# Revit family: Hager-VOLTA-Surface_mounted-IP30-Without_Cover-Without_DIN-Hosted-CH-fr
name_source: partatom
category: Electrical Equipment
units: mm (PartAtom-declared; Revit-internal decimal feet)

## family parameters
Cut with Voids When Loaded = No
Host = Face
Maintain Annotation Orientation = Yes
Panel Configuration = Two Columns, Circuits Across
Part Type = Panelboard
Room Calculation Point = No
Round Connector Dimension = Use Diameter
Shared = No

## types (1)
- VOLTA-Surface_mounted_W305_H640_D96_12_Modular_Spacing-VA48MD
    BC_MODEL_ID = 1547148
    BC_OBJECT_ID = 513473
    BC_OBJECT_VERSION = #9
    BC_VARIANT_ID = 1174158
    Code hager = ADD-EC000214_EU
    Default Elevation = 0 mm  [stored 0 ft]
    EF000003 - mode de montage = apparent
    EF000007 - couleur = blanc
    EF000008 - largeur = 305 mm  [stored 1.00066 ft]
    EF000024 - résiste aux UV = No
    EF000040 - hauteur = 640 mm  [stored 2.09974 ft]
    EF000049 - profondeur = 96 mm  [stored 0.314961 ft]
    EF000116 - numéro RAL = 9010
    EF000118 - avec plaque de montage = Yes
    EF000218 - profondeur de montage = 0 mm  [stored 0 ft]
    EF000266 - nombre de rangées = 4
    EF000332 - hauteur d'installation = 0 mm  [stored 0 ft]
    EF000846 - largeur d'encastrement = 0 mm  [stored 0 ft]
    EF001062 - version CEM = No
    EF001088 - possibilité de montage adossé = Yes
    EF001131 - profondeur interne = 0 mm  [stored 0 ft]
    EF001134 - rail DIN = No
    EF002950 - nombre d'unités modulaires = 12
    EF005474 - indice de protection (IP) = IP30
    EF006244 - couvercle/porte transparente = No
    EF006306 - avec serrure = No
    EF009212 - type de couvercle = avec découpe
    EF015776 - borne de mise à la terre = No
    EF015777 - borne à conducteur neutre = No
    EF015941 - porte de transmission du signal = No
    ETIM class code = EC000214
    ETIM class name = Small distribution board
    HG000001-nombre de colonnes = 0
    HG000002-avec porte = No
    HG000003-Gamme = VOLTA
    HG000004-Référence fabricant = VA48MD
    HG000005-Epaisseur = 2 mm  [stored 0.00656168 ft]
    HG000006-Encastré = No
    HG000007-Nombre de colonnes vides = 0
    HG000008-Nombre de rangées vides = 0
    HG000009-Porte à double battant = No
    HG000010-Portes asymétriques = No
    HG000011-Rangées du bas vides = No
    HG000012-Angle de pivotement de la porte = 90.00°
    HG000013-Porte à gauche = No
    HG000014-Porte à droite = Yes
    HG000015-Visibilité de l'emprise de la porte = Yes
    HG000016-Visibilité de la porte 3D = Yes
    HG000017-Distance entre pôles = 18 mm  [stored 0.0590551 ft]
    HG000060-RAL-number = 9010
    HG000099-ID modèle Onfly = 507532
    HGEF000266-Nombre de rangées = 4
    HGEF0002950-largeur en nombre de modules = 12
    Manufacturer = Hager
    Name = VOLTA-Surface_mounted-IP30-Without_Cover-Without_DIN-CH
    Name BIM&CO = Electricity
    Name hager = ADD_Enclosures_EC000214
    Reference = VOLTA-Surface_mounted_W305_H640_D96_12_Modular_Spacing-VA48MD
    Uniformat = Low Tension Service & Dist.
    Uniformat code = D501001

note: [stored X ft] marks values corroborated as IEEE doubles in the binary element streams (Revit-internal decimal feet)

## geometry (parser evidence)
native form markers: Sweep x14
no freeform markers — native parametric forms only
